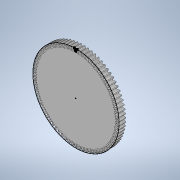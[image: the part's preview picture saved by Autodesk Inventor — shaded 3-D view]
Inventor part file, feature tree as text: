
AUTODESK INVENTOR PART (.ipt)
format: ipt  version: 2021 (Build 250183000, 183)  size: 503,808 bytes
history: native  units: in
note: dims shown in document units (in); Inventor stores cm internally (conversion verified against a paired STEP export)
features: extrude x4, sketch x3, pattern_circular x1, projected_geometry x1
ambient origin geometry x8: Origin, YZ Plane, XZ Plane, XY Plane, X Axis, Y Axis, Z Axis, Center Point
bodies: Solid1 (feature_tree)
feature tree (9):
  sketch  "Sketch1"  dims[d0=0.25in d1=0.0in]
  extrude  "Extrusion1"  TaperAngle=0.0deg  [1 undecoded]
  extrude  "Extrusion2"  Depth=29.5276in TaperAngle=360.0deg
  pattern_circular  "Circular Pattern1"  [2 undecoded]
  extrude  "Extrusion3"  Depth=0.5in
  extrude  "Extrusion4"  Depth=0.75in TaperAngle=0.0deg
  sketch  "Sketch2"  dims[d2=0.0in d3=0.0in d4=29.5276in d5=360.0deg]
  sketch  "Sketch3"  dims[d7=0.1875in d8=0.25in d9=0.0312in d10=0.75in d11=0.0in d12=0.5in d13=0.0in]
  projected_geometry  "Projected Loop1"
note: 3 required parameter values undecoded (feature->parameter linkage not recoverable at this tier; creation-order binding heuristic only, values carry confidence <= 0.55)
